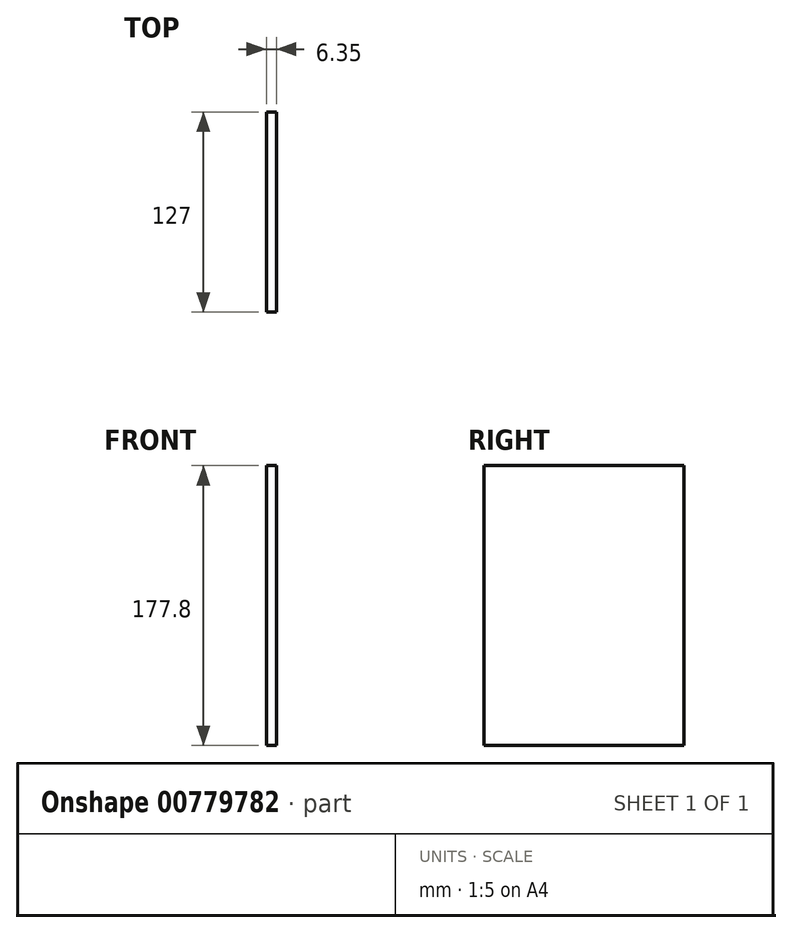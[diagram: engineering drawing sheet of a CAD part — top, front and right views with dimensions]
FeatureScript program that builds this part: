
annotation { "Feature Type Name" : "Feature", "Feature Type Description" : "" }
export const myFeature = defineFeature(function(context is Context, id is Id, definition is map)
    precondition{}
    {
        {
            var Q0;
            Q0=qCreatedBy(makeId("Right.planeOp"),FACE);
            var sketch = newSketch(context, id + "F0", { "sketchPlane" : qUnion([Q0])});
            skLineSegment(sketch, "E0.bottom", {"start": v(63.5, 88.9) * mm, "end": v(-63.5, 88.9) * mm});
            skLineSegment(sketch, "E0.top", {"start": v(63.5, -88.9) * mm, "end": v(-63.5, -88.9) * mm});
            skLineSegment(sketch, "E0.left", {"start": v(63.5, 88.9) * mm, "end": v(63.5, -88.9) * mm});
            skLineSegment(sketch, "E0.right", {"start": v(-63.5, 88.9) * mm, "end": v(-63.5, -88.9) * mm});
            skPoint(sketch, "E0.middle", {"position": v(0, 0) * mm});
            skSolve(sketch);
        }
        {
            var Q0;
            Q0 = qSketchRegion(id + "F0", true);
            extrude(context, id + "F1", {"entities" : qUnion([Q0]), "depth" : 6.35 * mm, "offsetDistance" : 25.4 * mm});
        }
    });
